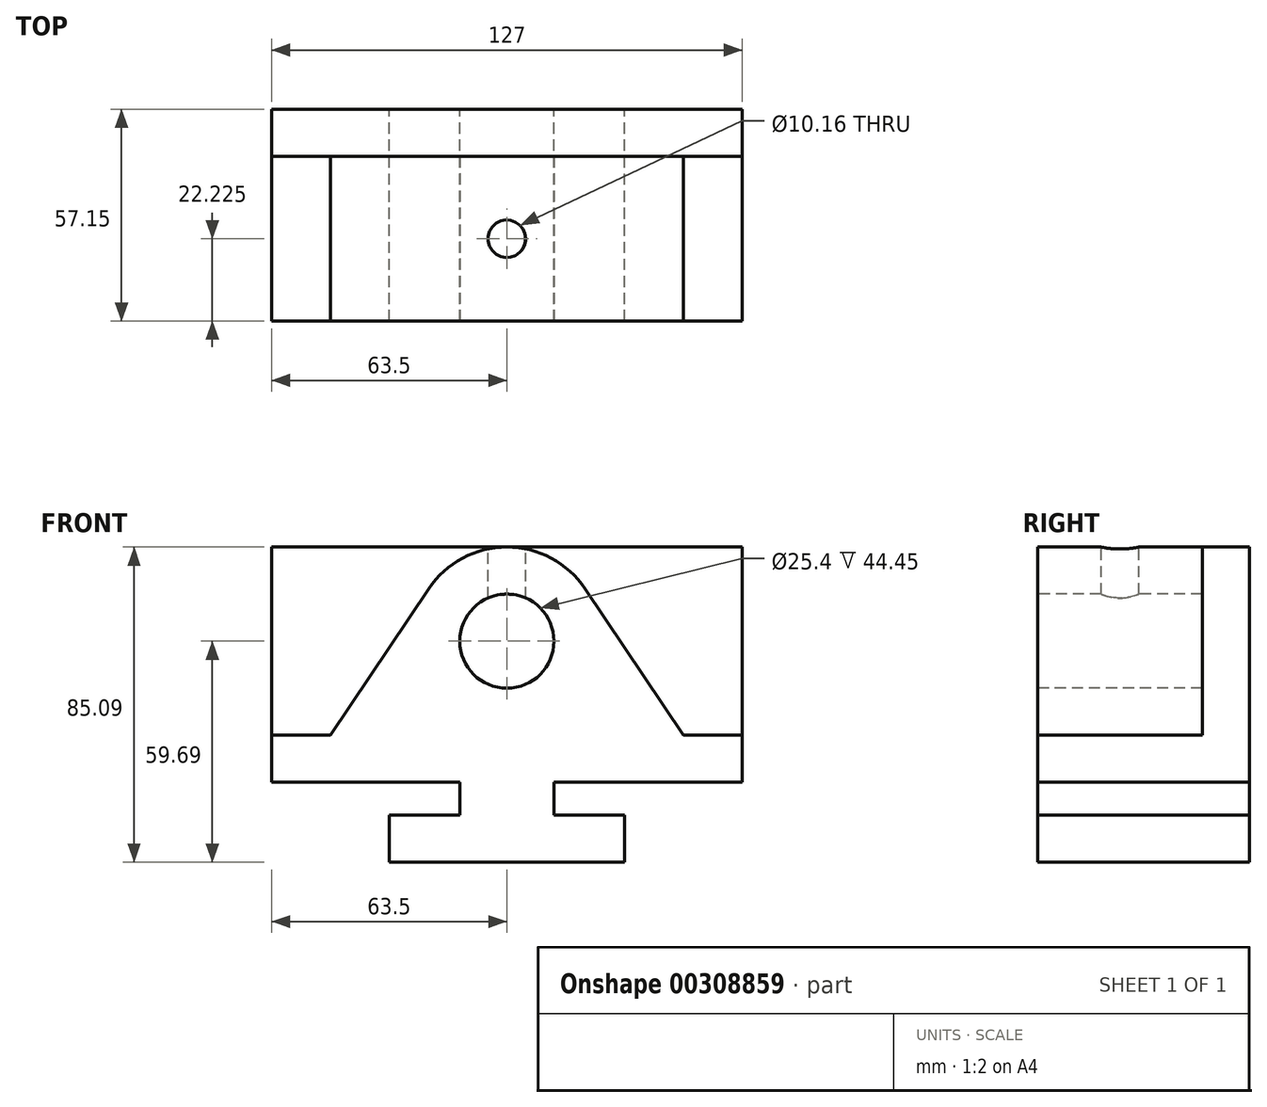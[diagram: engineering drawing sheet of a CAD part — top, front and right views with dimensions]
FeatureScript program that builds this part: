
annotation { "Feature Type Name" : "Feature", "Feature Type Description" : "" }
export const myFeature = defineFeature(function(context is Context, id is Id, definition is map)
    precondition{}
    {
        {
            var Q0;
            Q0=qCreatedBy(makeId("Front.planeOp"),FACE);
            var sketch = newSketch(context, id + "F0", { "sketchPlane" : qUnion([Q0])});
            skLineSegment(sketch, "E0", {"start": v(0, 0) * mm, "end": v(63.5, 0) * mm});
            skLineSegment(sketch, "E1", {"start": v(63.5, 0) * mm, "end": v(63.5, 12.7) * mm});
            skLineSegment(sketch, "E2", {"start": v(63.5, 12.7) * mm, "end": v(44.45, 12.7) * mm});
            skLineSegment(sketch, "E3", {"start": v(44.45, 12.7) * mm, "end": v(44.45, 21.59) * mm});
            skLineSegment(sketch, "E4", {"start": v(44.45, 21.59) * mm, "end": v(95.25, 21.59) * mm});
            skLineSegment(sketch, "E5", {"start": v(95.25, 21.59) * mm, "end": v(95.25, 85.1) * mm});
            skLineSegment(sketch, "E6", {"start": v(95.25, 85.1) * mm, "end": v(-31.75, 85.09) * mm});
            skLineSegment(sketch, "E7", {"start": v(-31.75, 85.1) * mm, "end": v(-31.75, 21.59) * mm});
            skLineSegment(sketch, "E8", {"start": v(-31.75, 21.59) * mm, "end": v(19.05, 21.59) * mm});
            skLineSegment(sketch, "E9", {"start": v(19.05, 21.59) * mm, "end": v(19.05, 12.7) * mm});
            skLineSegment(sketch, "E10", {"start": v(19.05, 12.7) * mm, "end": v(0, 12.7) * mm});
            skLineSegment(sketch, "E11", {"start": v(0, 12.7) * mm, "end": v(0, 0) * mm});
            skLineSegment(sketch, "E12", {"start": v(-31.75, 34.29) * mm, "end": v(-15.88, 34.29) * mm});
            skLineSegment(sketch, "E13", {"start": v(-15.88, 34.29) * mm, "end": v(10.66, 73.84) * mm});
            skLineSegment(sketch, "E14", {"start": v(95.25, 34.29) * mm, "end": v(79.38, 34.29) * mm});
            skLineSegment(sketch, "E15", {"start": v(79.38, 34.29) * mm, "end": v(52.84, 73.84) * mm});
            skArc(sketch, "E16", {"start": v(52.84, 73.84) * mm, "mid": v(31.75, 85.1) * mm, "end": v(10.66, 73.84) * mm});
            skSolve(sketch);
        }
        {
            var Q0;
            Q0 = qSketchRegion(id + "F0", true);
            extrude(context, id + "F1", {"entities" : qUnion([Q0]), "depth" : 57.15 * mm});
        }
        {
            var Q0;
            Q0=makeQuery(id+"F1.opExtrude","CAP_FACE",FACE,{"disambiguationData":[OSD([sQuery(id+"F0.wireOp",EDGE,"E0"),sQuery(id+"F0.wireOp",EDGE,"E1"),sQuery(id+"F0.wireOp",EDGE,"E2"),sQuery(id+"F0.wireOp",EDGE,"E3"),sQuery(id+"F0.wireOp",EDGE,"E4"),sQuery(id+"F0.wireOp",EDGE,"E5"),sQuery(id+"F0.wireOp",EDGE,"E6"),sQuery(id+"F0.wireOp",EDGE,"E7"),sQuery(id+"F0.wireOp",EDGE,"E8"),sQuery(id+"F0.wireOp",EDGE,"E9"),sQuery(id+"F0.wireOp",EDGE,"E10"),sQuery(id+"F0.wireOp",EDGE,"E11")])],"isStart":false});
            var sketch = newSketch(context, id + "F2", { "sketchPlane" : qUnion([Q0])});
            skLineSegment(sketch, "E17", {"start": v(-31.75, 34.3) * mm, "end": v(-15.87, 34.3) * mm});
            skLineSegment(sketch, "E18", {"start": v(-15.87, 34.3) * mm, "end": v(10.66, 73.84) * mm});
            skLineSegment(sketch, "E19", {"start": v(52.84, 73.84) * mm, "end": v(79.37, 34.3) * mm});
            skLineSegment(sketch, "E20", {"start": v(79.37, 34.3) * mm, "end": v(95.25, 34.3) * mm});
            skArc(sketch, "E21", {"start": v(52.84, 73.84) * mm, "mid": v(31.75, 85.1) * mm, "end": v(10.66, 73.84) * mm});
            skCircle(sketch, "E22", {"center": v(31.75, 59.69) * mm, "radius": 12.7 * mm});
            skSolve(sketch);
        }
        {
            var Q0;
            Q0 = qSketchRegion(id + "F2", true);
            var Q1;
            {var subQ1=sQuery(id+"F2.wireOp",EDGE,"E19");Q1=makeQuery(id+"F2.imprint","IMPRINT",FACE,{"disambiguationData":[TD([[makeQuery(id+"F2.imprint","IMPRINT",EDGE,{"derivedFrom":subQ1}),1.0]])]});}
            var Q2;
            {var subQ6=sQuery(id+"F2.wireOp",EDGE,"E17");Q2=makeQuery(id+"F2.imprint","IMPRINT",FACE,{"disambiguationData":[TD([[makeQuery(id+"F2.imprint","IMPRINT",EDGE,{"derivedFrom":subQ6}),1.0]])]});}
            extrude(context, id + "F3", {"entities" : qUnion([Q0, Q1, Q2]), "operationType" : NewBodyOperationType.REMOVE, "oppositeDirection" : true, "depth" : 44.45 * mm});
        }
        {
            var Q0;
            Q0=makeQuery(id+"F1.opExtrude","SWEPT_FACE",FACE,{"disambiguationData":[OSD([sQuery(id+"F0.wireOp",EDGE,"E6")])]});
            var sketch = newSketch(context, id + "F4", { "sketchPlane" : qUnion([Q0])});
            skLineSegment(sketch, "E23", {"start": v(31.75, 0) * mm, "end": v(31.75, -87.77) * mm, "construction": true});
            skCircle(sketch, "E24", {"center": v(31.75, -34.93) * mm, "radius": 5.08 * mm});
            skSolve(sketch);
        }
        {
            var Q0;
            Q0 = qSketchRegion(id + "F4", true);
            extrude(context, id + "F5", {"entities" : qUnion([Q0]), "operationType" : NewBodyOperationType.REMOVE, "oppositeDirection" : true, "depth" : 25.4 * mm});
        }
    });
